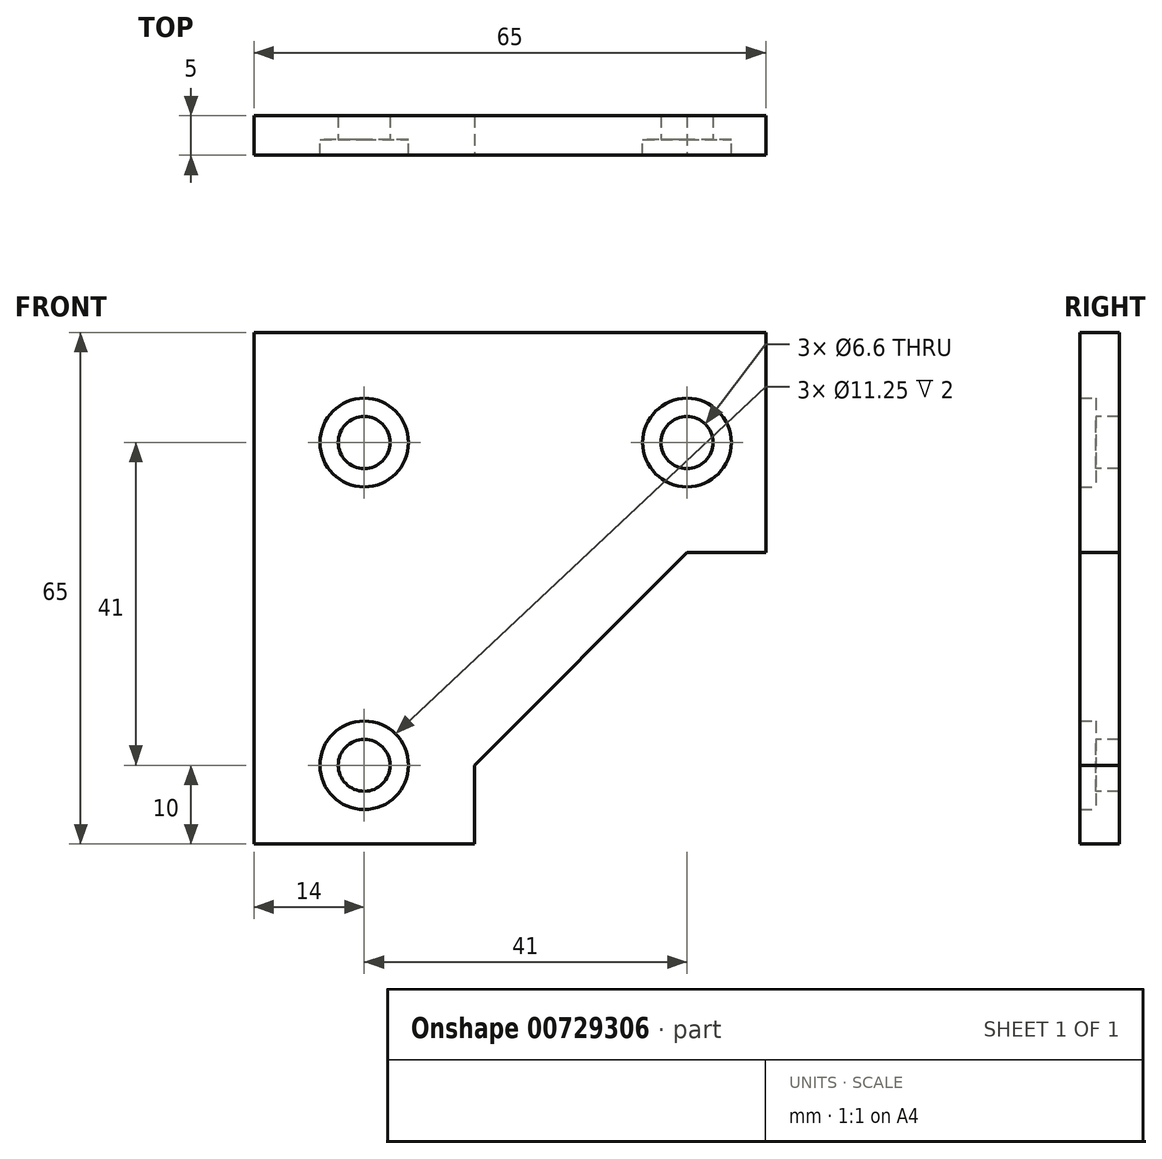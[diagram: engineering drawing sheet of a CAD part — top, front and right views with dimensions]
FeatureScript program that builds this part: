
annotation { "Feature Type Name" : "Feature", "Feature Type Description" : "" }
export const myFeature = defineFeature(function(context is Context, id is Id, definition is map)
    precondition{}
    {
        {
            var Q0;
            Q0=qCreatedBy(makeId("Front.planeOp"),FACE);
            var sketch = newSketch(context, id + "F0", { "sketchPlane" : qUnion([Q0])});
            skLineSegment(sketch, "E0", {"start": v(0, 0) * mm, "end": v(0, 65) * mm});
            skLineSegment(sketch, "E1", {"start": v(0, 65) * mm, "end": v(65, 65) * mm});
            skLineSegment(sketch, "E2", {"start": v(65, 65) * mm, "end": v(65, 37) * mm});
            skLineSegment(sketch, "E3", {"start": v(65, 37) * mm, "end": v(55, 37) * mm});
            skLineSegment(sketch, "E4", {"start": v(55, 37) * mm, "end": v(28, 10) * mm});
            skLineSegment(sketch, "E5", {"start": v(28, 10) * mm, "end": v(28, 0) * mm});
            skLineSegment(sketch, "E6", {"start": v(28, 0) * mm, "end": v(0, 0) * mm});
            skPoint(sketch, "E7", {"position": v(14, 51) * mm});
            skPoint(sketch, "E7.positionSnap0", {"position": v(14, 0) * mm});
            skPoint(sketch, "E7.positionSnap1", {"position": v(65, 51) * mm});
            skPoint(sketch, "E8", {"position": v(55, 51) * mm});
            skPoint(sketch, "E8.positionSnap0", {"position": v(60, 37) * mm});
            skPoint(sketch, "E9", {"position": v(14, 10) * mm});
            skPoint(sketch, "E9.positionSnap0", {"position": v(28, 5) * mm});
            skCircle(sketch, "E10", {"center": v(14, 51) * mm, "radius": 3.3 * mm});
            skCircle(sketch, "E11", {"center": v(55, 51) * mm, "radius": 3.3 * mm});
            skCircle(sketch, "E12", {"center": v(14, 10) * mm, "radius": 3.3 * mm});
            skSolve(sketch);
        }
        {
            var Q0;
            Q0=makeQuery(id+"F0.imprint","IMPRINT",FACE,{"disambiguationData":[TD([[makeQuery(id+"F0.imprint","IMPRINT",EDGE,{"derivedFrom":sQuery(id+"F0.wireOp",EDGE,"E0")}),-1.0]])]});
            extrude(context, id + "F1", {"entities" : qUnion([Q0]), "oppositeDirection" : true, "depth" : 5 * mm, "offsetDistance" : 25 * mm});
        }
        {
            var Q0;
            Q0=sQuery(id+"F0.wireOp",VERTEX,"E7");
            var Q1;
            Q1=sQuery(id+"F0.wireOp",VERTEX,"E8");
            var Q2;
            Q2=sQuery(id+"F0.wireOp",VERTEX,"E9");
            var Q3;
            Q3=makeQuery(id+"F1.opExtrude","SWEPT_BODY",BODY,{"disambiguationData":[OSD([sQuery(id+"F0.wireOp",EDGE,"E0"),sQuery(id+"F0.wireOp",EDGE,"E1"),sQuery(id+"F0.wireOp",EDGE,"E2"),sQuery(id+"F0.wireOp",EDGE,"E3"),sQuery(id+"F0.wireOp",EDGE,"E4"),sQuery(id+"F0.wireOp",EDGE,"E5"),sQuery(id+"F0.wireOp",EDGE,"E6"),sQuery(id+"F0.wireOp",EDGE,"E10"),sQuery(id+"F0.wireOp",EDGE,"E11"),sQuery(id+"F0.wireOp",EDGE,"E12")])]});
            hole(context, id + "F2", {"style" : HoleStyle.C_BORE, "endStyle" : HoleEndStyle.BLIND, "holeDiameter" : 6.6 * mm, "cBoreDiameter" : 11.25 * mm, "cBoreDepth" : 2 * mm, "majorDiameter" : 5 * mm, "holeDepth" : 20 * mm, "isTappedThrough" : true, "tappedDepth" : 12 * mm, "tapClearance" : 3, "locations" : qUnion([Q0, Q1, Q2]), "scope" : qUnion([Q3])});
        }
    });
